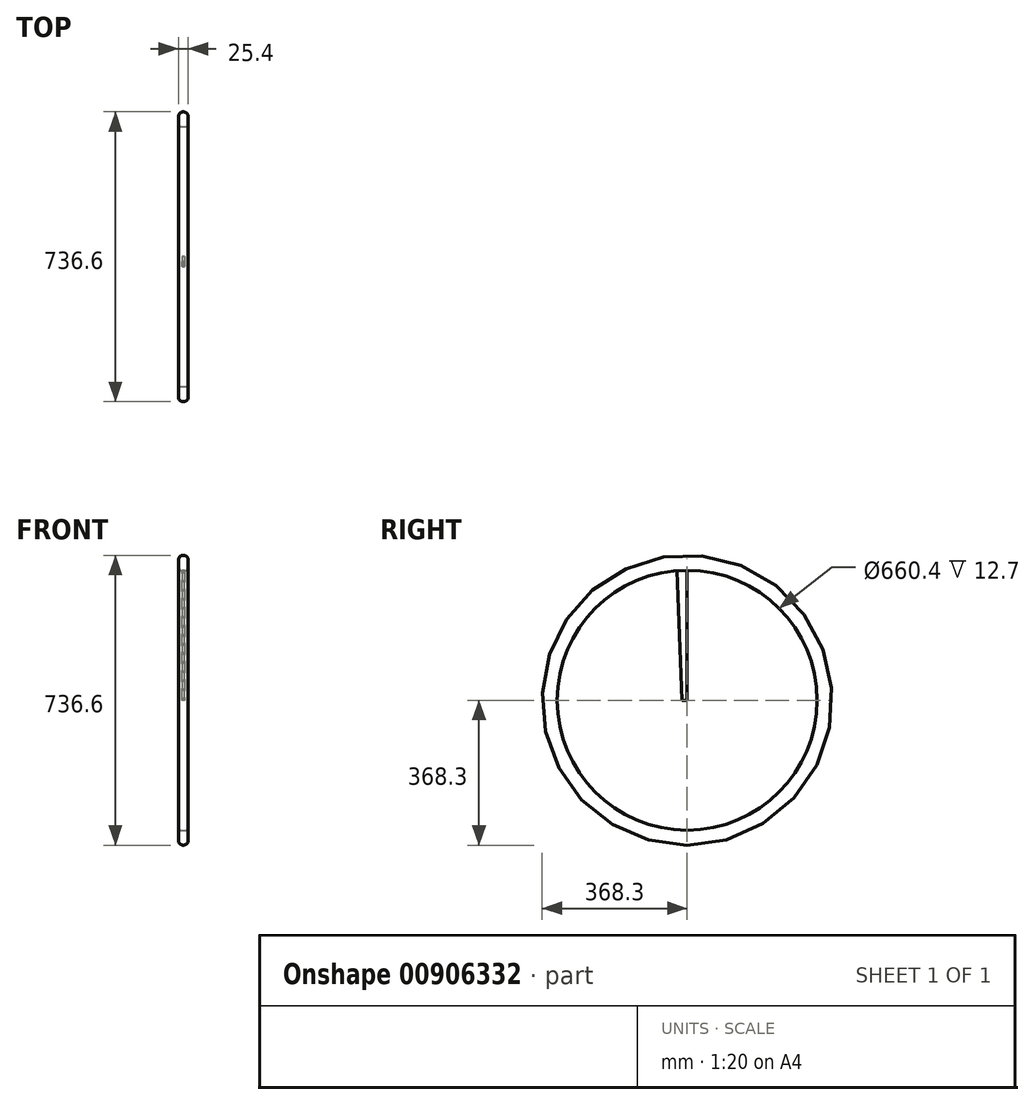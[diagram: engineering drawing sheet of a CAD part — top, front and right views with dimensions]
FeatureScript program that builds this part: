
annotation { "Feature Type Name" : "Feature", "Feature Type Description" : "" }
export const myFeature = defineFeature(function(context is Context, id is Id, definition is map)
    precondition{}
    {
        {
            var Q0;
            Q0=qCreatedBy(makeId("Front.planeOp"),FACE);
            var sketch = newSketch(context, id + "F0", { "sketchPlane" : qUnion([Q0])});
            skLineSegment(sketch, "E0", {"start": v(0, 0) * mm, "end": v(0, 330.2) * mm, "construction": true});
            skLineSegment(sketch, "E1", {"start": v(-6.35, 330.2) * mm, "end": v(6.35, 330.2) * mm});
            skLineSegment(sketch, "E2", {"start": v(-12.7, 336.55) * mm, "end": v(-12.7, 355.6) * mm});
            skLineSegment(sketch, "E3", {"start": v(12.7, 336.55) * mm, "end": v(12.7, 355.6) * mm});
            skLineSegment(sketch, "E4", {"start": v(0, 368.3) * mm, "end": v(0, 368.3) * mm});
            skPoint(sketch, "E5.visualSharp", {"position": v(12.7, 330.2) * mm});
            skPoint(sketch, "E6.visualSharp", {"position": v(-12.7, 330.2) * mm});
            skPoint(sketch, "E7.visualSharp", {"position": v(12.7, 368.3) * mm});
            skArc(sketch, "E7.filletArc", {"start": v(12.7, 355.6) * mm, "mid": v(8.98, 364.58) * mm, "end": v(0, 368.3) * mm});
            skPoint(sketch, "E8.visualSharp", {"position": v(-12.7, 368.3) * mm});
            skArc(sketch, "E8.filletArc", {"start": v(0, 368.3) * mm, "mid": v(-8.98, 364.58) * mm, "end": v(-12.7, 355.6) * mm});
            skArc(sketch, "E9.filletArc", {"start": v(-12.7, 336.55) * mm, "mid": v(-10.84, 332.06) * mm, "end": v(-6.35, 330.2) * mm});
            skArc(sketch, "E10.filletArc", {"start": v(6.35, 330.2) * mm, "mid": v(10.84, 332.06) * mm, "end": v(12.7, 336.55) * mm});
            skLineSegment(sketch, "E11", {"start": v(0, 0) * mm, "end": v(-181.7, 0) * mm, "construction": true});
            skSolve(sketch);
        }
        {
            var Q0;
            Q0=makeQuery(id+"F0.imprint","IMPRINT",FACE,{"disambiguationData":[TD([[makeQuery(id+"F0.imprint","IMPRINT",EDGE,{"derivedFrom":sQuery(id+"F0.wireOp",EDGE,"E1")}),1.0]])]});
            var Q1;
            Q1=sQuery(id+"F0.wireOp",EDGE,"E11");
            revolve(context, id + "F1", {"surfaceOperationType" : NewSurfaceOperationType.NEW, "entities" : qUnion([Q0]), "axis" : qUnion([Q1]), "revolveType" : RevolveType.FULL});
        }
        {
            var Q0;
            Q0=qCreatedBy(makeId("Right.planeOp"),FACE);
            var sketch = newSketch(context, id + "F2", { "sketchPlane" : qUnion([Q0])});
            skLineSegment(sketch, "E12", {"start": v(0, 0) * mm, "end": v(0, 330.2) * mm});
            skLineSegment(sketch, "E13", {"start": v(-25.4, 330.2) * mm, "end": v(-12.7, 0) * mm});
            skLineSegment(sketch, "E14", {"start": v(0, 330.2) * mm, "end": v(-76.55, 330.2) * mm, "construction": true});
            skLineSegment(sketch, "E15", {"start": v(-25.4, 330.2) * mm, "end": v(0, 330.2) * mm});
            skLineSegment(sketch, "E16", {"start": v(0, 0) * mm, "end": v(-12.7, 0) * mm});
            skSolve(sketch);
        }
        {
            var Q0;
            Q0 = qSketchRegion(id + "F2", true);
            extrude(context, id + "F3", {"entities" : qUnion([Q0]), "operationType" : NewBodyOperationType.ADD, "endBound" : BoundingType.SYMMETRIC, "depth" : 6.35 * mm, "offsetDistance" : 25.4 * mm});
        }
    });
